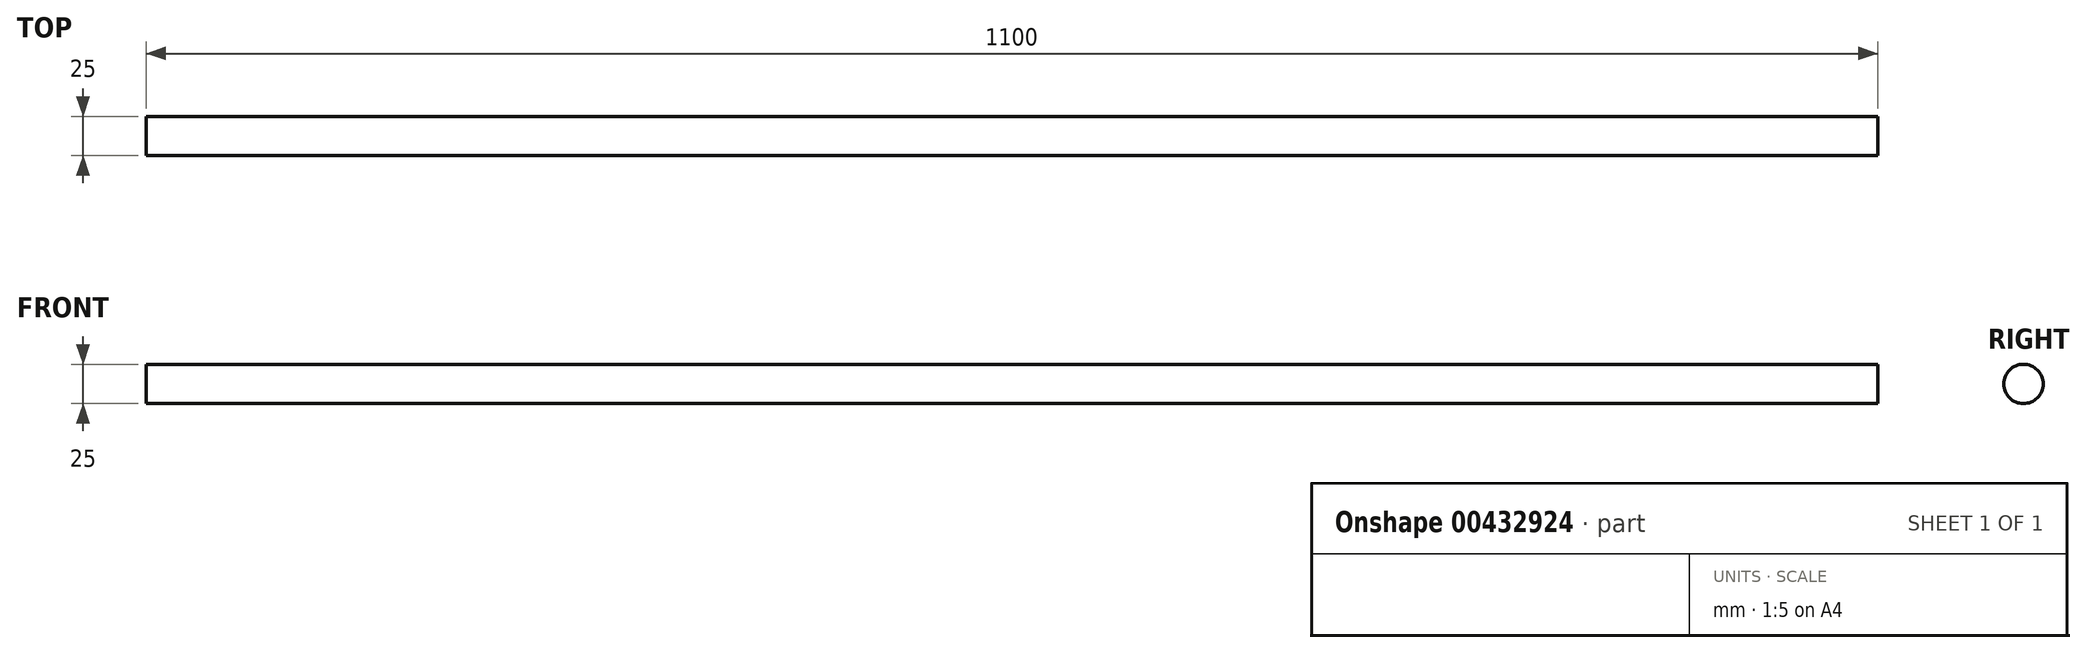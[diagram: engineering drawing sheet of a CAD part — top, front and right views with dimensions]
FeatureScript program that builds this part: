
annotation { "Feature Type Name" : "Feature", "Feature Type Description" : "" }
export const myFeature = defineFeature(function(context is Context, id is Id, definition is map)
    precondition{}
    {
        {
            var Q0;
            Q0=qCreatedBy(makeId("Right.planeOp"),FACE);
            var sketch = newSketch(context, id + "F0", { "sketchPlane" : qUnion([Q0])});
            skCircle(sketch, "E0", {"center": v(0, 0) * mm, "radius": 12.5 * mm});
            skSolve(sketch);
        }
        {
            var Q0;
            Q0=makeQuery(id+"F0.imprint","IMPRINT",FACE,{"disambiguationData":[TD([[makeQuery(id+"F0.imprint","IMPRINT",EDGE,{"derivedFrom":sQuery(id+"F0.wireOp",EDGE,"E0")}),1.0]])]});
            extrude(context, id + "F1", {"entities" : qUnion([Q0]), "depth" : 1100 * mm});
        }
    });
